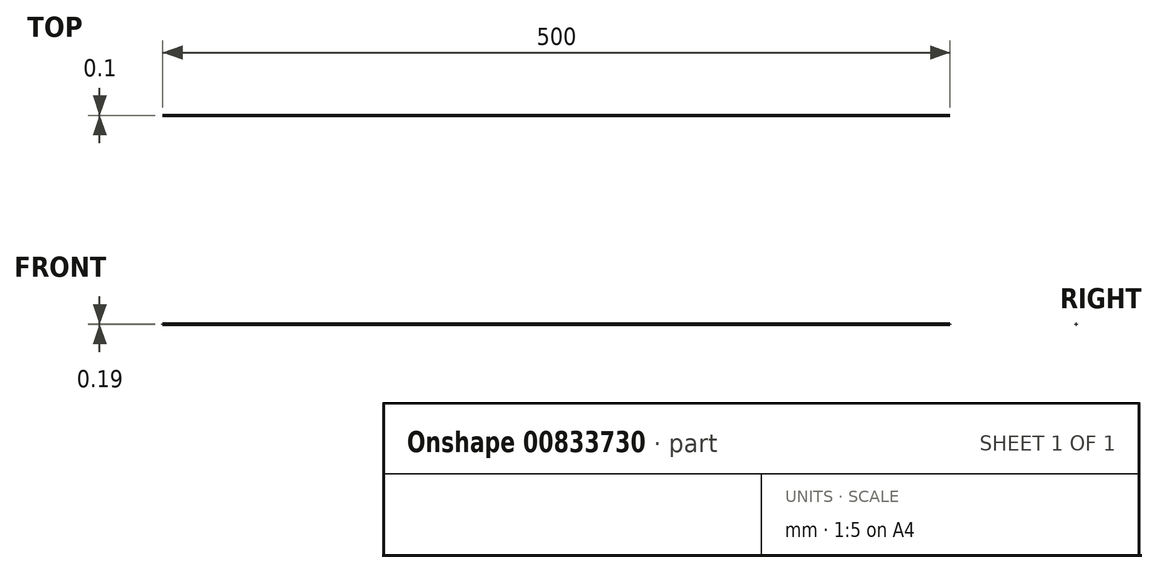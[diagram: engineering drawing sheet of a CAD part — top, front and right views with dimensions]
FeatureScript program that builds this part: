
annotation { "Feature Type Name" : "Feature", "Feature Type Description" : "" }
export const myFeature = defineFeature(function(context is Context, id is Id, definition is map)
    precondition{}
    {
        {
            var Q0;
            Q0=qCreatedBy(makeId("Right.planeOp"),FACE);
            var sketch = newSketch(context, id + "F0", { "sketchPlane" : qUnion([Q0])});
            skLineSegment(sketch, "E0", {"start": v(-0.05, 0.08) * mm, "end": v(0.05, 0.08) * mm});
            skLineSegment(sketch, "E1", {"start": v(0.05, 0.08) * mm, "end": v(0.05, 0) * mm});
            skLineSegment(sketch, "E2", {"start": v(0.05, 0) * mm, "end": v(0.02, 0) * mm});
            skLineSegment(sketch, "E3", {"start": v(0.02, 0) * mm, "end": v(0.02, -0.11) * mm});
            skLineSegment(sketch, "E4", {"start": v(0.02, -0.11) * mm, "end": v(-0.02, -0.11) * mm});
            skLineSegment(sketch, "E5", {"start": v(-0.02, -0.11) * mm, "end": v(-0.02, 0) * mm});
            skLineSegment(sketch, "E6", {"start": v(-0.02, 0) * mm, "end": v(-0.05, 0) * mm});
            skLineSegment(sketch, "E7", {"start": v(-0.05, 0) * mm, "end": v(-0.05, 0.08) * mm});
            skSolve(sketch);
        }
        {
            var Q0;
            Q0 = qSketchRegion(id + "F0", true);
            extrude(context, id + "F1", {"entities" : qUnion([Q0]), "depth" : 500 * mm, "offsetDistance" : 25 * mm});
        }
    });
